# Revit family: Shower-Receptor-STERLING-OC-S-63-62061100
name_source: partatom
category: Plumbing Fixtures
revit_build: Autodesk Revit 2015 (Build: 20140606_1530(x64)
units: mm (PartAtom-declared; Revit-internal decimal feet)

## types (2) — shared parameters
ADA Compliant = Yes
Assembly Code = D2010700
CW Connection = No
Cold Water Inlet = Cold Water Inlet
Date Modified = 11/09/2017
Default Elevation = 0"
Description = Series 6206, 63-1/4inch x 39-3/8inch Roll-in Shower Receptor
HW Connection = No
Height = 8"
Hot Water Inlet = Hot Water Inlet
Length = 63 1/4"
Manufacturer = Sterling
MasterFormat 1995 = 15410
MasterFormat 2004 = 22.41.23
Material = Vikrell material
Panel Thickness = 0"
Product Documentation Link = https://resources.kohler.com
Product Name = Roll-in Shower OC-S-63
Product Page URL = http://www.sterlingplumbing.com
URL = https://www.sterlingplumbing.com
Vent Connection = No
Waste Connection = Yes
Waste Water Outlet = Waste Water Outlet
Width = 39 3/8"

## per-type parameters (varying)
| type | Finish | Model | Type |
| 0-White | Kohler-Vikrell-0-White | 62061100-0 | 1 |
| 96-Biscuit | Kohler-Vikrell-96-Biscuit | 62061100-96 | 2 |

## geometry (parser evidence)
native form markers: Sweep x5
no freeform markers — native parametric forms only
